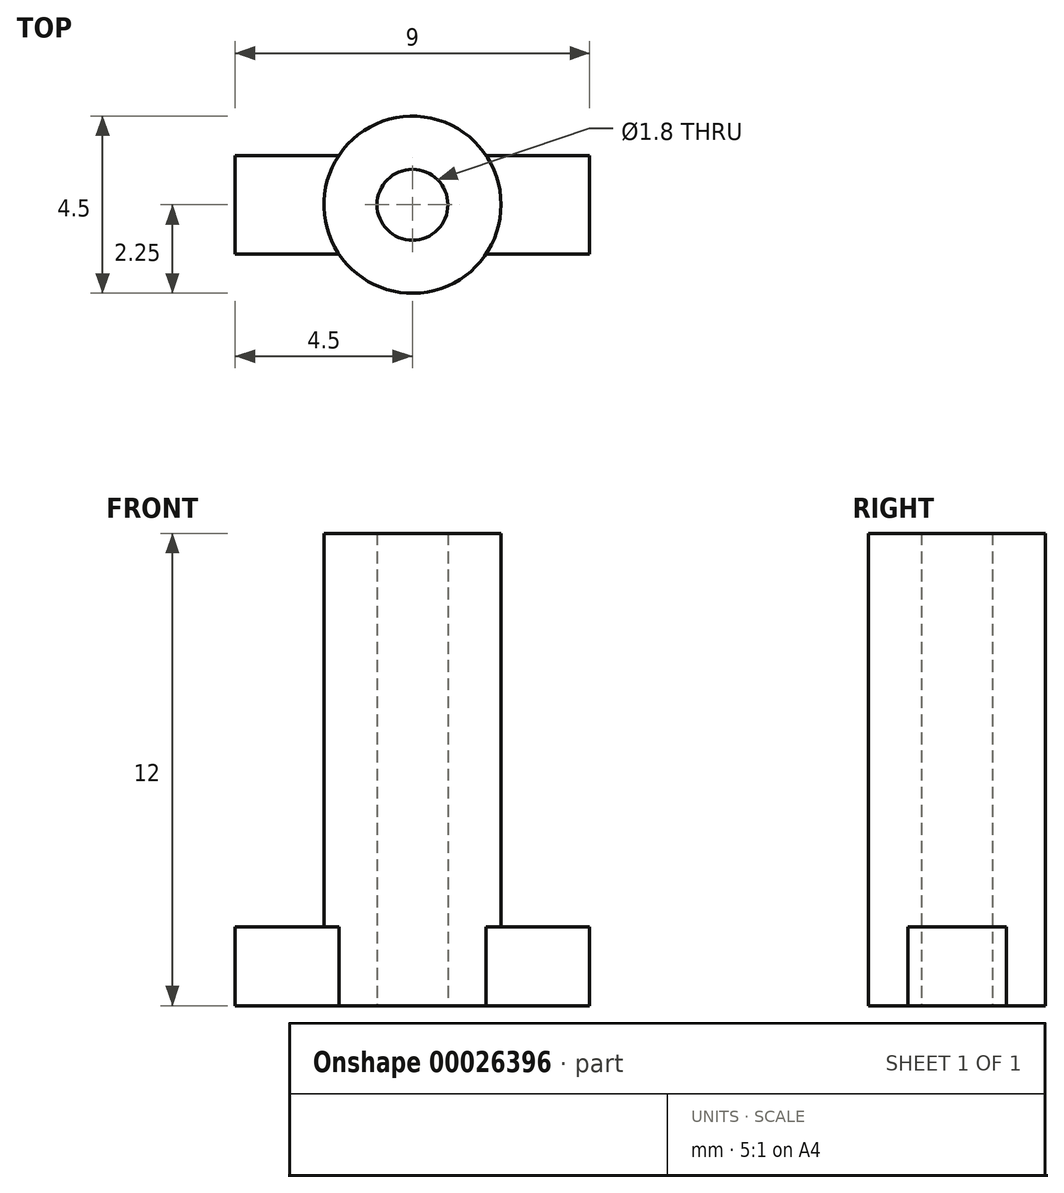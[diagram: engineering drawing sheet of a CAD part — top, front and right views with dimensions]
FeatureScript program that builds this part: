
annotation { "Feature Type Name" : "Feature", "Feature Type Description" : "" }
export const myFeature = defineFeature(function(context is Context, id is Id, definition is map)
    precondition{}
    {
        {
            var Q0;
            Q0=qCreatedBy(makeId("Top.planeOp"),FACE);
            var sketch = newSketch(context, id + "F0", { "sketchPlane" : qUnion([Q0])});
            skCircle(sketch, "E0", {"center": v(0, 0) * mm, "radius": 0.9 * mm});
            skCircle(sketch, "E1", {"center": v(0, 0) * mm, "radius": 2.25 * mm});
            skSolve(sketch);
        }
        {
            var Q0;
            Q0=makeQuery(id+"F0.imprint","IMPRINT",FACE,{"disambiguationData":[TD([[makeQuery(id+"F0.imprint","IMPRINT",EDGE,{"derivedFrom":sQuery(id+"F0.wireOp",EDGE,"E0")}),-1.0]])]});
            extrude(context, id + "F1", {"entities" : qUnion([Q0]), "depth" : 12 * mm});
        }
        {
            var Q0;
            Q0=makeQuery(id+"F1.opExtrude","CAP_FACE",FACE,{"disambiguationData":[OSD([sQuery(id+"F0.wireOp",EDGE,"E0"),sQuery(id+"F0.wireOp",EDGE,"E1")])],"isStart":true});
            var sketch = newSketch(context, id + "F2", { "sketchPlane" : qUnion([Q0])});
            skLineSegment(sketch, "E2.bottom", {"start": v(-4.5, 1.25) * mm, "end": v(4.5, 1.25) * mm});
            skLineSegment(sketch, "E2.top", {"start": v(-4.5, -1.25) * mm, "end": v(4.5, -1.25) * mm});
            skLineSegment(sketch, "E2.left", {"start": v(-4.5, 1.25) * mm, "end": v(-4.5, -1.25) * mm});
            skLineSegment(sketch, "E2.right", {"start": v(4.5, 1.25) * mm, "end": v(4.5, -1.25) * mm});
            skSolve(sketch);
        }
        {
            var Q0;
            {var subQ0=sQuery(id+"F2.wireOp",EDGE,"E2.left");Q0=makeQuery(id+"F2.imprint","IMPRINT",FACE,{"disambiguationData":[TD([[makeQuery(id+"F2.imprint","IMPRINT",EDGE,{"derivedFrom":subQ0}),1.0]])]});}
            var Q1;
            {var subQ0=sQuery(id+"F2.wireOp",EDGE,"E2.right");Q1=makeQuery(id+"F2.imprint","IMPRINT",FACE,{"disambiguationData":[TD([[makeQuery(id+"F2.imprint","IMPRINT",EDGE,{"derivedFrom":subQ0}),-1.0]])]});}
            extrude(context, id + "F3", {"entities" : qUnion([Q0, Q1]), "operationType" : NewBodyOperationType.ADD, "oppositeDirection" : true, "depth" : 2 * mm});
        }
    });
